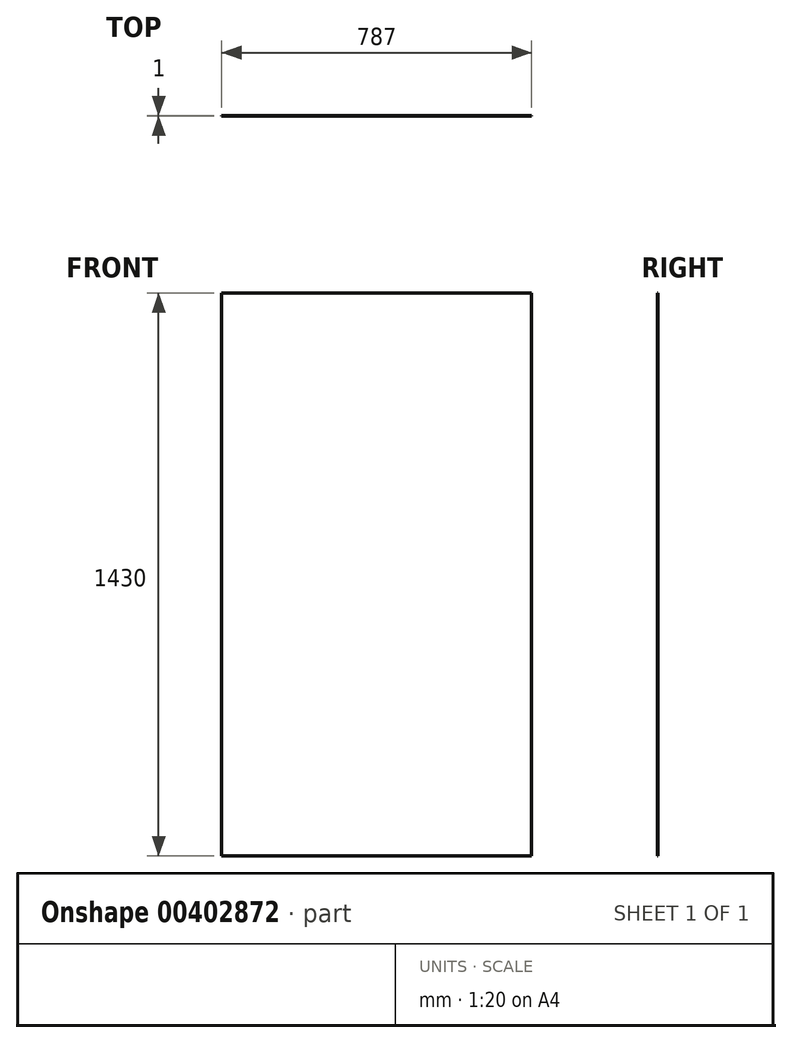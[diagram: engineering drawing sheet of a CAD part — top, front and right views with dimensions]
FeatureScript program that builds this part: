
annotation { "Feature Type Name" : "Feature", "Feature Type Description" : "" }
export const myFeature = defineFeature(function(context is Context, id is Id, definition is map)
    precondition{}
    {
        {
            var Q0;
            Q0=qCreatedBy(makeId("Front.planeOp"),FACE);
            var sketch = newSketch(context, id + "F0", { "sketchPlane" : qUnion([Q0])});
            skLineSegment(sketch, "E0.bottom", {"start": v(-393.5, 715) * mm, "end": v(393.5, 715) * mm});
            skLineSegment(sketch, "E0.top", {"start": v(-393.5, -715) * mm, "end": v(393.5, -715) * mm});
            skLineSegment(sketch, "E0.left", {"start": v(-393.5, 715) * mm, "end": v(-393.5, -715) * mm});
            skLineSegment(sketch, "E0.right", {"start": v(393.5, 715) * mm, "end": v(393.5, -715) * mm});
            skPoint(sketch, "E0.middle", {"position": v(0, 0) * mm});
            skSolve(sketch);
        }
        {
            var Q0;
            Q0=makeQuery(id+"F0.imprint","IMPRINT",FACE,{"disambiguationData":[TD([[makeQuery(id+"F0.imprint","IMPRINT",EDGE,{"derivedFrom":sQuery(id+"F0.wireOp",EDGE,"E0.bottom")}),-1.0]])]});
            extrude(context, id + "F1", {"entities" : qUnion([Q0]), "depth" : 1 * mm});
        }
    });
